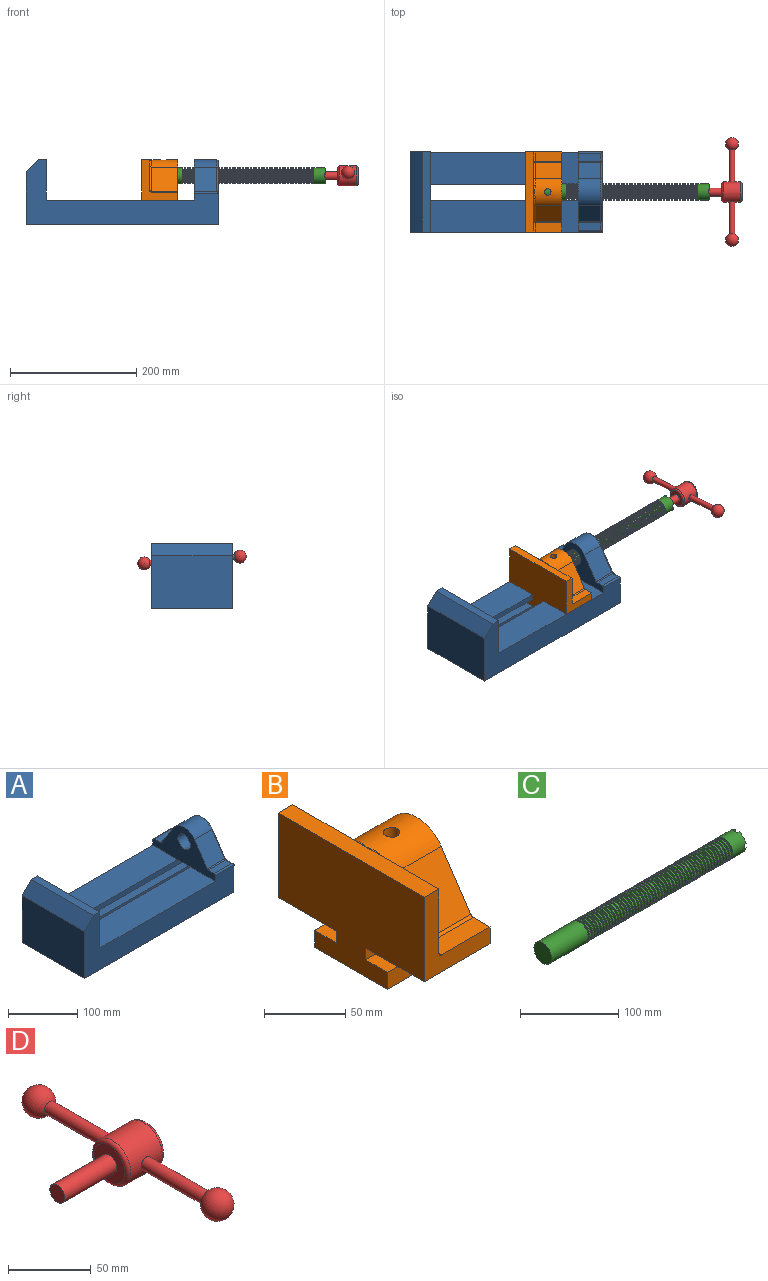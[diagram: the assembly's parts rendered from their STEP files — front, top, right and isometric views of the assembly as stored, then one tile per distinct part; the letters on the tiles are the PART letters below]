
ASSEMBLY  parts=4 mates=4
PART A: 39 faces, bbox 304.8x127x103.7 mm
  f0: plane 234.95x50.8mm, normal (0,0,1), area 11935.5mm2, adj f3,f8,f16,f26
  f1: plane 127x99.06mm, normal (1,0,0), area 7097.5mm2, adj f7,f8,f9,f14,f17,f18,f19,f20
  f2: plane 234.95x50.8mm, normal (0,0,1), area 11935.5mm2, adj f3,f9,f16,f27
  f3: plane 127x101.6mm, normal (1,0,0), area 9516.1mm2, adj f0,f2,f4,f7,f8,f9,f18,f19
  f4: plane 127x12.7mm, normal (0,0,1), area 1612.9mm2, adj f3,f5,f8,f9
  f5: plane 127x19.05mm, normal (-0.71,0,0.71), area 3421.5mm2, adj f4,f6,f8,f9
  f6: plane 127x82.55mm, normal (-1,0,0), area 10483.8mm2, adj f5,f7,f8,f9
  f7: plane 304.8x127mm, normal (0,0,-1), area 31774.1mm2, adj f1,f3,f6,f8,f9,f21,f22
  f8: plane 304.8x101.6mm, normal (0,-1,0), area 13834.6mm2, adj f0,f1,f3,f4,f5,f6,f7,f16
  f9: plane 304.8x101.6mm, normal (0,1,0), area 13834.6mm2, adj f1,f2,f3,f4,f5,f6,f7,f16
  f10: plane 35.56x11.98mm, normal (0,0,1), area 426mm2, adj f16,f28,f29,f30
  f11: plane 38.43x35.56mm, normal (0,0.83,0.56), area 1645.4mm2, adj f12,f16,f29,f32
  f12: cylinder r=25.4mm len=42.19mm, axis (1,0,0), area 1770.2mm2, adj f11,f13,f16,f33
  f13: plane 38.43x35.56mm, normal (0,-0.83,0.56), area 1645.4mm2, adj f12,f16,f34,f35
  f14: cylinder r=12.7mm len=38.1mm, axis (1,0,0), area 3040.2mm2, adj f1,f16
  f15: plane 35.56x11.98mm, normal (0,0,1), area 426mm2, adj f16,f34,f36,f38
  f16: plane 127x63.5mm, normal (-1,0,0), area 4155.5mm2, adj f0,f2,f8,f9,f10,f11,f12,f13
  f17: plane 38.1x25.4mm, normal (0,0,-1), area 967.7mm2, adj f1,f16,f26,f27
  f18: plane 273.05x19.05mm, normal (0,0,-1), area 5201.6mm2, adj f1,f3,f19,f26
  f19: plane 273.05x12.7mm, normal (0,1,0), area 3467.7mm2, adj f1,f3,f18,f20
  f20: plane 273.05x19.05mm, normal (0,0,1), area 5201.6mm2, adj f1,f3,f19,f21
  f21: plane 273.05x16.51mm, normal (0,1,0), area 4508.1mm2, adj f1,f3,f7,f20
  f22: plane 273.05x16.51mm, normal (0,-1,0), area 4508.1mm2, adj f1,f3,f7,f23
  f23: plane 273.05x19.05mm, normal (0,0,1), area 5201.6mm2, adj f1,f3,f22,f24
  f24: plane 273.05x12.7mm, normal (0,-1,0), area 3467.7mm2, adj f1,f3,f23,f25
  f25: plane 273.05x19.05mm, normal (0,0,-1), area 5201.6mm2, adj f1,f3,f24,f27
  f26: plane 273.05x8.89mm, normal (0,1,0), area 2427.4mm2, adj f0,f1,f3,f17,f18
  f27: plane 273.05x8.89mm, normal (0,-1,0), area 2427.4mm2, adj f1,f2,f3,f17,f25
  f28: cylinder r=2.54mm len=38.1mm, axis (1,0,0), area 148.3mm2, adj f9,f10,f16,f30
  f29: cylinder r=2.54mm len=35.56mm, axis (-1,0,0), area 88.5mm2, adj f10,f11,f16,f31
  f30: cylinder r=2.54mm len=14.52mm, axis (0,1,0), area 54.3mm2, adj f1,f10,f28,f31
  f31: torus R=5.08mm, axis (-1,0,0), area 13.5mm2, adj f1,f29,f30,f32
  f32: cylinder r=2.54mm len=39.84mm, axis (0,0.56,-0.83), area 184.6mm2, adj f1,f11,f31,f33
  f33: torus R=22.86mm, axis (-1,0,0), area 191.4mm2, adj f1,f12,f32,f35
  f34: cylinder r=2.54mm len=35.56mm, axis (-1,0,0), area 88.5mm2, adj f13,f15,f16,f37
  f35: cylinder r=2.54mm len=39.84mm, axis (0,0.56,0.83), area 184.6mm2, adj f1,f13,f33,f37
  f36: cylinder r=2.54mm len=38.1mm, axis (-1,0,0), area 148.3mm2, adj f8,f15,f16,f38
  f37: torus R=5.08mm, axis (-1,0,0), area 13.5mm2, adj f1,f34,f35,f38
  f38: cylinder r=2.54mm len=14.52mm, axis (0,1,0), area 54.3mm2, adj f1,f15,f36,f37
PART B: 36 faces, bbox 57.2x127x89 mm
  f0: plane 57.15x50.8mm, normal (0,0,-1), area 2903.2mm2, adj f6,f9,f10,f23
  f1: cylinder r=12.7mm len=44.45mm, axis (1,0,0), area 3464.3mm2, adj f6,f15,f16
  f2: plane 41.91x14.52mm, normal (0,0,1), area 608.5mm2, adj f6,f11,f24,f25
  f3: plane 51.86x48.26mm, normal (1,0,0), area 1495.7mm2, adj f8,f10,f31,f33,f35
  f4: plane 51.86x48.26mm, normal (1,0,0), area 1495.7mm2, adj f8,f11,f24,f28,f29
  f5: plane 57.15x50.8mm, normal (0,0,-1), area 2903.2mm2, adj f6,f9,f11,f22
  f6: plane 127x85.09mm, normal (1,0,0), area 5190.6mm2, adj f0,f1,f2,f5,f7,f10,f11,f12
  f7: plane 41.91x14.52mm, normal (0,0,1), area 608.5mm2, adj f6,f10,f30,f31
  f8: plane 127x12.7mm, normal (0,0,1), area 1612.9mm2, adj f3,f4,f9,f10,f11,f26,f34
  f9: plane 127x85.09mm, normal (-1,0,0), area 9096.8mm2, adj f0,f5,f8,f10,f11,f17,f18,f19
  f10: plane 63.5x57.15mm, normal (0,-1,0), area 1372.3mm2, adj f0,f3,f6,f7,f8,f9,f31
  f11: plane 63.5x57.15mm, normal (0,1,0), area 1372.3mm2, adj f2,f4,f5,f6,f8,f9,f24
  f12: plane 41.91x38.43mm, normal (0,-0.83,0.56), area 1939.2mm2, adj f6,f13,f30,f33
  f13: cylinder r=25.4mm len=44.45mm, axis (1,0,0), area 2026.5mm2, adj f6,f12,f14,f16,f26,f28,f34,f35
  f14: plane 41.91x38.43mm, normal (0,0.83,0.56), area 1939.2mm2, adj f6,f13,f25,f29
  f15: plane 25.4x25.4mm, normal (1,0,0), area 506.7mm2, adj f1
  f16: cylinder r=5.08mm len=13.76mm, axis (0,0,1), area 414mm2, adj f1,f13
  f17: plane 57.15x19.05mm, normal (0,0,1), area 1088.7mm2, adj f6,f9,f18,f23
  f18: plane 57.15x12.7mm, normal (0,-1,0), area 725.8mm2, adj f6,f9,f17,f19
  f19: plane 63.5x57.15mm, normal (0,0,-1), area 3629mm2, adj f6,f9,f18,f20
  f20: plane 57.15x12.7mm, normal (0,1,0), area 725.8mm2, adj f6,f9,f19,f21
  f21: plane 57.15x19.05mm, normal (0,0,1), area 1088.7mm2, adj f6,f9,f20,f22
  f22: plane 57.15x8.89mm, normal (0,1,0), area 508.1mm2, adj f5,f6,f9,f21
  f23: plane 57.15x8.89mm, normal (0,-1,0), area 508.1mm2, adj f0,f6,f9,f17
  f24: cylinder r=2.54mm len=14.52mm, axis (0,-1,0), area 57.9mm2, adj f2,f4,f11,f27
  f25: cylinder r=2.54mm len=41.91mm, axis (1,0,0), area 104.3mm2, adj f2,f6,f14,f27
  f26: bspline ~12.24x2.8mm, area 20.9mm2, adj f8,f13,f28
  f27: sphere r=2.54mm, area 6.3mm2, adj f24,f25,f29
  f28: torus R=27.94mm, axis (1,0,0), area 57.8mm2, adj f4,f13,f26,f29
  f29: cylinder r=2.54mm len=39.84mm, axis (0,-0.56,0.83), area 184.6mm2, adj f4,f14,f27,f28
  f30: cylinder r=2.54mm len=41.91mm, axis (1,0,0), area 104.3mm2, adj f6,f7,f12,f32
  f31: cylinder r=2.54mm len=14.52mm, axis (0,-1,0), area 57.9mm2, adj f3,f7,f10,f32
  f32: sphere r=2.54mm, area 6.3mm2, adj f30,f31,f33
  f33: cylinder r=2.54mm len=39.84mm, axis (0,-0.56,-0.83), area 184.6mm2, adj f3,f12,f32,f35
  f34: bspline ~12.24x2.8mm, area 20.9mm2, adj f8,f13,f35
  f35: torus R=27.94mm, axis (1,0,0), area 57.8mm2, adj f3,f13,f33,f34
PART C: 220 faces, bbox 279.4x25.4x25.4 mm
  f0: cylinder r=12.7mm len=25.4mm, axis (-1,0,0), area 1468.2mm2, adj f1,f2,f3,f5,f7,f208,f209,f210
  f1: plane 9.9x9.9mm, normal (1,0,0), area 62.3mm2, adj f0,f4,f213,f216
  f2: plane 9.9x9.9mm, normal (1,0,0), area 62.3mm2, adj f0,f4,f210,f218
  f3: plane 9.9x9.9mm, normal (1,0,0), area 62.3mm2, adj f0,f4,f209,f212
  f4: cylinder r=6.35mm len=25.4mm, axis (1,0,0), area 960.3mm2, adj f1,f2,f3,f5,f6,f208,f209,f210
  f5: plane 9.9x9.9mm, normal (1,0,0), area 62.3mm2, adj f0,f4,f215,f217
  f6: plane 12.7x12.7mm, normal (1,0,0), area 126.7mm2, adj f4
  f7: cone r=12.7mm half-angle=76deg, axis (1,0,0), area 188mm2, adj f0,f9
  f8: cone r=10.16mm half-angle=76deg, axis (-1,0,0), area 188mm2, adj f9,f10
  f9: cylinder r=10.16mm len=20.32mm, axis (1,0,0), area 81.1mm2, adj f7,f8
  f10: cylinder r=12.7mm len=25.4mm, axis (-1,0,0), area 131.7mm2, adj f8,f11
  f11: cone r=12.7mm half-angle=76deg, axis (1,0,0), area 188mm2, adj f10,f13
  f12: cone r=10.16mm half-angle=76deg, axis (-1,0,0), area 188mm2, adj f13,f14
  f13: cylinder r=10.16mm len=20.32mm, axis (1,0,0), area 81.1mm2, adj f11,f12
  f14: cylinder r=12.7mm len=25.4mm, axis (-1,0,0), area 131.7mm2, adj f12,f15
  f15: cone r=12.7mm half-angle=76deg, axis (1,0,0), area 188mm2, adj f14,f17
  f16: cone r=10.16mm half-angle=76deg, axis (-1,0,0), area 188mm2, adj f17,f18
  f17: cylinder r=10.16mm len=20.32mm, axis (1,0,0), area 81.1mm2, adj f15,f16
  f18: cylinder r=12.7mm len=25.4mm, axis (-1,0,0), area 131.7mm2, adj f16,f19
  f19: cone r=12.7mm half-angle=76deg, axis (1,0,0), area 188mm2, adj f18,f21
  f20: cone r=10.16mm half-angle=76deg, axis (-1,0,0), area 188mm2, adj f21,f22
  f21: cylinder r=10.16mm len=20.32mm, axis (1,0,0), area 81.1mm2, adj f19,f20
  f22: cylinder r=12.7mm len=25.4mm, axis (-1,0,0), area 131.7mm2, adj f20,f23
  f23: cone r=12.7mm half-angle=76deg, axis (1,0,0), area 188mm2, adj f22,f25
  f24: cone r=10.16mm half-angle=76deg, axis (-1,0,0), area 188mm2, adj f25,f26
  f25: cylinder r=10.16mm len=20.32mm, axis (1,0,0), area 81.1mm2, adj f23,f24
  f26: cylinder r=12.7mm len=25.4mm, axis (-1,0,0), area 131.7mm2, adj f24,f27
  f27: cone r=12.7mm half-angle=76deg, axis (1,0,0), area 188mm2, adj f26,f29
  f28: cone r=10.16mm half-angle=76deg, axis (-1,0,0), area 188mm2, adj f29,f30
  f29: cylinder r=10.16mm len=20.32mm, axis (1,0,0), area 81.1mm2, adj f27,f28
  f30: cylinder r=12.7mm len=25.4mm, axis (-1,0,0), area 131.7mm2, adj f28,f31
  f31: cone r=12.7mm half-angle=76deg, axis (1,0,0), area 188mm2, adj f30,f33
  f32: cone r=10.16mm half-angle=76deg, axis (-1,0,0), area 188mm2, adj f33,f34
  f33: cylinder r=10.16mm len=20.32mm, axis (1,0,0), area 81.1mm2, adj f31,f32
  f34: cylinder r=12.7mm len=25.4mm, axis (-1,0,0), area 131.7mm2, adj f32,f35
  f35: cone r=12.7mm half-angle=76deg, axis (1,0,0), area 188mm2, adj f34,f37
  f36: cone r=10.16mm half-angle=76deg, axis (-1,0,0), area 188mm2, adj f37,f38
  f37: cylinder r=10.16mm len=20.32mm, axis (1,0,0), area 81.1mm2, adj f35,f36
  f38: cylinder r=12.7mm len=25.4mm, axis (-1,0,0), area 131.7mm2, adj f36,f39
  f39: cone r=12.7mm half-angle=76deg, axis (1,0,0), area 188mm2, adj f38,f41
  f40: cone r=10.16mm half-angle=76deg, axis (-1,0,0), area 188mm2, adj f41,f42
  f41: cylinder r=10.16mm len=20.32mm, axis (1,0,0), area 81.1mm2, adj f39,f40
  f42: cylinder r=12.7mm len=25.4mm, axis (-1,0,0), area 131.7mm2, adj f40,f43
  f43: cone r=12.7mm half-angle=76deg, axis (1,0,0), area 188mm2, adj f42,f45
  f44: cone r=10.16mm half-angle=76deg, axis (-1,0,0), area 188mm2, adj f45,f46
  f45: cylinder r=10.16mm len=20.32mm, axis (1,0,0), area 81.1mm2, adj f43,f44
  f46: cylinder r=12.7mm len=25.4mm, axis (-1,0,0), area 131.7mm2, adj f44,f47
  f47: cone r=12.7mm half-angle=76deg, axis (1,0,0), area 188mm2, adj f46,f49
  f48: cone r=10.16mm half-angle=76deg, axis (-1,0,0), area 188mm2, adj f49,f50
  f49: cylinder r=10.16mm len=20.32mm, axis (1,0,0), area 81.1mm2, adj f47,f48
  f50: cylinder r=12.7mm len=25.4mm, axis (-1,0,0), area 131.7mm2, adj f48,f51
  f51: cone r=12.7mm half-angle=76deg, axis (1,0,0), area 188mm2, adj f50,f53
  f52: cone r=10.16mm half-angle=76deg, axis (-1,0,0), area 188mm2, adj f53,f54
  f53: cylinder r=10.16mm len=20.32mm, axis (1,0,0), area 81.1mm2, adj f51,f52
  f54: cylinder r=12.7mm len=25.4mm, axis (-1,0,0), area 131.7mm2, adj f52,f55
  f55: cone r=12.7mm half-angle=76deg, axis (1,0,0), area 188mm2, adj f54,f57
  f56: cone r=10.16mm half-angle=76deg, axis (-1,0,0), area 188mm2, adj f57,f58
  f57: cylinder r=10.16mm len=20.32mm, axis (1,0,0), area 81.1mm2, adj f55,f56
  f58: cylinder r=12.7mm len=25.4mm, axis (-1,0,0), area 131.7mm2, adj f56,f59
  f59: cone r=12.7mm half-angle=76deg, axis (1,0,0), area 188mm2, adj f58,f61
  f60: cone r=10.16mm half-angle=76deg, axis (-1,0,0), area 188mm2, adj f61,f62
  f61: cylinder r=10.16mm len=20.32mm, axis (1,0,0), area 81.1mm2, adj f59,f60
  f62: cylinder r=12.7mm len=25.4mm, axis (-1,0,0), area 131.7mm2, adj f60,f63
  f63: cone r=12.7mm half-angle=76deg, axis (1,0,0), area 188mm2, adj f62,f65
  f64: cone r=10.16mm half-angle=76deg, axis (-1,0,0), area 188mm2, adj f65,f66
  f65: cylinder r=10.16mm len=20.32mm, axis (1,0,0), area 81.1mm2, adj f63,f64
  f66: cylinder r=12.7mm len=25.4mm, axis (-1,0,0), area 131.7mm2, adj f64,f67
  f67: cone r=12.7mm half-angle=76deg, axis (1,0,0), area 188mm2, adj f66,f69
  f68: cone r=10.16mm half-angle=76deg, axis (-1,0,0), area 188mm2, adj f69,f70
  f69: cylinder r=10.16mm len=20.32mm, axis (1,0,0), area 81.1mm2, adj f67,f68
  f70: cylinder r=12.7mm len=25.4mm, axis (-1,0,0), area 131.7mm2, adj f68,f71
  f71: cone r=12.7mm half-angle=76deg, axis (1,0,0), area 188mm2, adj f70,f73
  f72: cone r=10.16mm half-angle=76deg, axis (-1,0,0), area 188mm2, adj f73,f74
  f73: cylinder r=10.16mm len=20.32mm, axis (1,0,0), area 81.1mm2, adj f71,f72
  f74: cylinder r=12.7mm len=25.4mm, axis (-1,0,0), area 131.7mm2, adj f72,f75
  f75: cone r=12.7mm half-angle=76deg, axis (1,0,0), area 188mm2, adj f74,f77
  f76: cone r=10.16mm half-angle=76deg, axis (-1,0,0), area 188mm2, adj f77,f78
  f77: cylinder r=10.16mm len=20.32mm, axis (1,0,0), area 81.1mm2, adj f75,f76
  f78: cylinder r=12.7mm len=25.4mm, axis (-1,0,0), area 131.7mm2, adj f76,f79
  f79: cone r=12.7mm half-angle=76deg, axis (1,0,0), area 188mm2, adj f78,f81
  f80: cone r=10.16mm half-angle=76deg, axis (-1,0,0), area 188mm2, adj f81,f82
  f81: cylinder r=10.16mm len=20.32mm, axis (1,0,0), area 81.1mm2, adj f79,f80
  f82: cylinder r=12.7mm len=25.4mm, axis (-1,0,0), area 131.7mm2, adj f80,f83
  f83: cone r=12.7mm half-angle=76deg, axis (1,0,0), area 188mm2, adj f82,f85
  f84: cone r=10.16mm half-angle=76deg, axis (-1,0,0), area 188mm2, adj f85,f86
  f85: cylinder r=10.16mm len=20.32mm, axis (1,0,0), area 81.1mm2, adj f83,f84
  f86: cylinder r=12.7mm len=25.4mm, axis (-1,0,0), area 131.7mm2, adj f84,f87
  f87: cone r=12.7mm half-angle=76deg, axis (1,0,0), area 188mm2, adj f86,f89
  f88: cone r=10.16mm half-angle=76deg, axis (-1,0,0), area 188mm2, adj f89,f90
  f89: cylinder r=10.16mm len=20.32mm, axis (1,0,0), area 81.1mm2, adj f87,f88
  f90: cylinder r=12.7mm len=25.4mm, axis (-1,0,0), area 131.7mm2, adj f88,f91
  f91: cone r=12.7mm half-angle=76deg, axis (1,0,0), area 188mm2, adj f90,f93
  f92: cone r=10.16mm half-angle=76deg, axis (-1,0,0), area 188mm2, adj f93,f94
  f93: cylinder r=10.16mm len=20.32mm, axis (1,0,0), area 81.1mm2, adj f91,f92
  f94: cylinder r=12.7mm len=25.4mm, axis (-1,0,0), area 131.7mm2, adj f92,f95
  f95: cone r=12.7mm half-angle=76deg, axis (1,0,0), area 188mm2, adj f94,f97
  f96: cone r=10.16mm half-angle=76deg, axis (-1,0,0), area 188mm2, adj f97,f98
  f97: cylinder r=10.16mm len=20.32mm, axis (1,0,0), area 81.1mm2, adj f95,f96
  f98: cylinder r=12.7mm len=25.4mm, axis (-1,0,0), area 131.7mm2, adj f96,f99
  f99: cone r=12.7mm half-angle=76deg, axis (1,0,0), area 188mm2, adj f98,f101
  f100: cone r=10.16mm half-angle=76deg, axis (-1,0,0), area 188mm2, adj f101,f102
  f101: cylinder r=10.16mm len=20.32mm, axis (1,0,0), area 81.1mm2, adj f99,f100
  f102: cylinder r=12.7mm len=25.4mm, axis (-1,0,0), area 131.7mm2, adj f100,f103
  f103: cone r=12.7mm half-angle=76deg, axis (1,0,0), area 188mm2, adj f102,f105
  f104: cone r=10.16mm half-angle=76deg, axis (-1,0,0), area 188mm2, adj f105,f106
  f105: cylinder r=10.16mm len=20.32mm, axis (1,0,0), area 81.1mm2, adj f103,f104
  f106: cylinder r=12.7mm len=25.4mm, axis (-1,0,0), area 131.7mm2, adj f104,f107
  f107: cone r=12.7mm half-angle=76deg, axis (1,0,0), area 188mm2, adj f106,f109
  f108: cone r=10.16mm half-angle=76deg, axis (-1,0,0), area 188mm2, adj f109,f110
  f109: cylinder r=10.16mm len=20.32mm, axis (1,0,0), area 81.1mm2, adj f107,f108
  f110: cylinder r=12.7mm len=25.4mm, axis (-1,0,0), area 131.7mm2, adj f108,f111
  f111: cone r=12.7mm half-angle=76deg, axis (1,0,0), area 188mm2, adj f110,f113
  f112: cone r=10.16mm half-angle=76deg, axis (-1,0,0), area 188mm2, adj f113,f114
  f113: cylinder r=10.16mm len=20.32mm, axis (1,0,0), area 81.1mm2, adj f111,f112
  f114: cylinder r=12.7mm len=25.4mm, axis (-1,0,0), area 131.7mm2, adj f112,f115
  f115: cone r=12.7mm half-angle=76deg, axis (1,0,0), area 188mm2, adj f114,f117
  f116: cone r=10.16mm half-angle=76deg, axis (-1,0,0), area 188mm2, adj f117,f118
  f117: cylinder r=10.16mm len=20.32mm, axis (1,0,0), area 81.1mm2, adj f115,f116
  f118: cylinder r=12.7mm len=25.4mm, axis (-1,0,0), area 131.7mm2, adj f116,f119
  f119: cone r=12.7mm half-angle=76deg, axis (1,0,0), area 188mm2, adj f118,f121
  f120: cone r=10.16mm half-angle=76deg, axis (-1,0,0), area 188mm2, adj f121,f122
  f121: cylinder r=10.16mm len=20.32mm, axis (1,0,0), area 81.1mm2, adj f119,f120
  f122: cylinder r=12.7mm len=25.4mm, axis (-1,0,0), area 131.7mm2, adj f120,f123
  f123: cone r=12.7mm half-angle=76deg, axis (1,0,0), area 188mm2, adj f122,f125
  f124: cone r=10.16mm half-angle=76deg, axis (-1,0,0), area 188mm2, adj f125,f126
  f125: cylinder r=10.16mm len=20.32mm, axis (1,0,0), area 81.1mm2, adj f123,f124
  f126: cylinder r=12.7mm len=25.4mm, axis (-1,0,0), area 131.7mm2, adj f124,f127
  f127: cone r=12.7mm half-angle=76deg, axis (1,0,0), area 188mm2, adj f126,f129
  f128: cone r=10.16mm half-angle=76deg, axis (-1,0,0), area 188mm2, adj f129,f130
  f129: cylinder r=10.16mm len=20.32mm, axis (1,0,0), area 81.1mm2, adj f127,f128
  f130: cylinder r=12.7mm len=25.4mm, axis (-1,0,0), area 131.7mm2, adj f128,f131
  f131: cone r=12.7mm half-angle=76deg, axis (1,0,0), area 188mm2, adj f130,f133
  f132: cone r=10.16mm half-angle=76deg, axis (-1,0,0), area 188mm2, adj f133,f134
  f133: cylinder r=10.16mm len=20.32mm, axis (1,0,0), area 81.1mm2, adj f131,f132
  f134: cylinder r=12.7mm len=25.4mm, axis (-1,0,0), area 131.7mm2, adj f132,f135
  f135: cone r=12.7mm half-angle=76deg, axis (1,0,0), area 188mm2, adj f134,f137
  f136: cone r=10.16mm half-angle=76deg, axis (-1,0,0), area 188mm2, adj f137,f138
  f137: cylinder r=10.16mm len=20.32mm, axis (1,0,0), area 81.1mm2, adj f135,f136
  f138: cylinder r=12.7mm len=25.4mm, axis (-1,0,0), area 131.7mm2, adj f136,f139
  f139: cone r=12.7mm half-angle=76deg, axis (1,0,0), area 188mm2, adj f138,f141
  f140: cone r=10.16mm half-angle=76deg, axis (-1,0,0), area 188mm2, adj f141,f142
  f141: cylinder r=10.16mm len=20.32mm, axis (1,0,0), area 81.1mm2, adj f139,f140
  f142: cylinder r=12.7mm len=25.4mm, axis (-1,0,0), area 131.7mm2, adj f140,f143
  f143: cone r=12.7mm half-angle=76deg, axis (1,0,0), area 188mm2, adj f142,f145
  f144: cone r=10.16mm half-angle=76deg, axis (-1,0,0), area 188mm2, adj f145,f146
  f145: cylinder r=10.16mm len=20.32mm, axis (1,0,0), area 81.1mm2, adj f143,f144
  f146: cylinder r=12.7mm len=25.4mm, axis (-1,0,0), area 131.7mm2, adj f144,f147
  f147: cone r=12.7mm half-angle=76deg, axis (1,0,0), area 188mm2, adj f146,f149
  f148: cone r=10.16mm half-angle=76deg, axis (-1,0,0), area 188mm2, adj f149,f150
  f149: cylinder r=10.16mm len=20.32mm, axis (1,0,0), area 81.1mm2, adj f147,f148
  f150: cylinder r=12.7mm len=25.4mm, axis (-1,0,0), area 131.7mm2, adj f148,f151
  f151: cone r=12.7mm half-angle=76deg, axis (1,0,0), area 188mm2, adj f150,f153
  f152: cone r=10.16mm half-angle=76deg, axis (-1,0,0), area 188mm2, adj f153,f154
  f153: cylinder r=10.16mm len=20.32mm, axis (1,0,0), area 81.1mm2, adj f151,f152
  f154: cylinder r=12.7mm len=25.4mm, axis (-1,0,0), area 131.7mm2, adj f152,f155
  f155: cone r=12.7mm half-angle=76deg, axis (1,0,0), area 188mm2, adj f154,f157
  f156: cone r=10.16mm half-angle=76deg, axis (-1,0,0), area 188mm2, adj f157,f158
  f157: cylinder r=10.16mm len=20.32mm, axis (1,0,0), area 81.1mm2, adj f155,f156
  f158: cylinder r=12.7mm len=25.4mm, axis (-1,0,0), area 131.7mm2, adj f156,f159
  f159: cone r=12.7mm half-angle=76deg, axis (1,0,0), area 188mm2, adj f158,f161
  f160: cone r=10.16mm half-angle=76deg, axis (-1,0,0), area 188mm2, adj f161,f162
  f161: cylinder r=10.16mm len=20.32mm, axis (1,0,0), area 81.1mm2, adj f159,f160
  f162: cylinder r=12.7mm len=25.4mm, axis (-1,0,0), area 131.7mm2, adj f160,f163
  f163: cone r=12.7mm half-angle=76deg, axis (1,0,0), area 188mm2, adj f162,f165
  f164: cone r=10.16mm half-angle=76deg, axis (-1,0,0), area 188mm2, adj f165,f166
  f165: cylinder r=10.16mm len=20.32mm, axis (1,0,0), area 81.1mm2, adj f163,f164
  f166: cylinder r=12.7mm len=25.4mm, axis (-1,0,0), area 131.7mm2, adj f164,f167
  f167: cone r=12.7mm half-angle=76deg, axis (1,0,0), area 188mm2, adj f166,f169
  f168: cone r=10.16mm half-angle=76deg, axis (-1,0,0), area 188mm2, adj f169,f170
  f169: cylinder r=10.16mm len=20.32mm, axis (1,0,0), area 81.1mm2, adj f167,f168
  f170: cylinder r=12.7mm len=25.4mm, axis (-1,0,0), area 131.7mm2, adj f168,f171
  f171: cone r=12.7mm half-angle=76deg, axis (1,0,0), area 188mm2, adj f170,f173
  f172: cone r=10.16mm half-angle=76deg, axis (-1,0,0), area 188mm2, adj f173,f174
  f173: cylinder r=10.16mm len=20.32mm, axis (1,0,0), area 81.1mm2, adj f171,f172
  f174: cylinder r=12.7mm len=25.4mm, axis (-1,0,0), area 131.7mm2, adj f172,f175
  f175: cone r=12.7mm half-angle=76deg, axis (1,0,0), area 188mm2, adj f174,f177
  f176: cone r=10.16mm half-angle=76deg, axis (-1,0,0), area 188mm2, adj f177,f178
  f177: cylinder r=10.16mm len=20.32mm, axis (1,0,0), area 81.1mm2, adj f175,f176
  f178: cylinder r=12.7mm len=25.4mm, axis (-1,0,0), area 131.7mm2, adj f176,f179
  f179: cone r=12.7mm half-angle=76deg, axis (1,0,0), area 188mm2, adj f178,f181
  f180: cone r=10.16mm half-angle=76deg, axis (-1,0,0), area 188mm2, adj f181,f182
  f181: cylinder r=10.16mm len=20.32mm, axis (1,0,0), area 81.1mm2, adj f179,f180
  f182: cylinder r=12.7mm len=25.4mm, axis (-1,0,0), area 131.7mm2, adj f180,f183
  f183: cone r=12.7mm half-angle=76deg, axis (1,0,0), area 188mm2, adj f182,f185
  f184: cone r=10.16mm half-angle=76deg, axis (-1,0,0), area 188mm2, adj f185,f186
  f185: cylinder r=10.16mm len=20.32mm, axis (1,0,0), area 81.1mm2, adj f183,f184
  f186: cylinder r=12.7mm len=25.4mm, axis (-1,0,0), area 131.7mm2, adj f184,f187
  f187: cone r=12.7mm half-angle=76deg, axis (1,0,0), area 188mm2, adj f186,f189
  f188: cone r=10.16mm half-angle=76deg, axis (-1,0,0), area 188mm2, adj f189,f190
  f189: cylinder r=10.16mm len=20.32mm, axis (1,0,0), area 81.1mm2, adj f187,f188
  f190: cylinder r=12.7mm len=25.4mm, axis (-1,0,0), area 131.7mm2, adj f188,f191
  f191: cone r=12.7mm half-angle=76deg, axis (1,0,0), area 188mm2, adj f190,f193
  f192: cone r=10.16mm half-angle=76deg, axis (-1,0,0), area 188mm2, adj f193,f194
  f193: cylinder r=10.16mm len=20.32mm, axis (1,0,0), area 81.1mm2, adj f191,f192
  f194: cylinder r=12.7mm len=25.4mm, axis (-1,0,0), area 131.7mm2, adj f192,f195
  f195: cone r=12.7mm half-angle=76deg, axis (1,0,0), area 188mm2, adj f194,f197
  f196: cone r=10.16mm half-angle=76deg, axis (-1,0,0), area 188mm2, adj f197,f198
  f197: cylinder r=10.16mm len=20.32mm, axis (1,0,0), area 81.1mm2, adj f195,f196
  f198: cylinder r=12.7mm len=25.4mm, axis (-1,0,0), area 131.7mm2, adj f196,f199
  f199: cone r=12.7mm half-angle=76deg, axis (1,0,0), area 188mm2, adj f198,f201
  f200: cone r=10.16mm half-angle=76deg, axis (-1,0,0), area 188mm2, adj f201,f202
  f201: cylinder r=10.16mm len=20.32mm, axis (1,0,0), area 81.1mm2, adj f199,f200
  f202: cylinder r=12.7mm len=25.4mm, axis (-1,0,0), area 131.7mm2, adj f200,f203
  f203: cone r=12.7mm half-angle=76deg, axis (1,0,0), area 188mm2, adj f202,f205
  f204: cone r=10.16mm half-angle=76deg, axis (-1,0,0), area 188mm2, adj f205,f207
  f205: cylinder r=10.16mm len=20.32mm, axis (1,0,0), area 81.1mm2, adj f203,f204
  f206: plane 25.4x25.4mm, normal (-1,0,0), area 506.7mm2, adj f207
  f207: cylinder r=12.7mm len=52.45mm, axis (-1,0,0), area 4185.4mm2, adj f204,f206
  f208: plane 6.88x5.08mm, normal (1,0,0), area 32.7mm2, adj f0,f4,f209,f210
  f209: plane 6.62x2.54mm, normal (0,-1,0), area 16.8mm2, adj f0,f3,f4,f208
  f210: plane 6.62x2.54mm, normal (0,1,0), area 16.8mm2, adj f0,f2,f4,f208
  f211: plane 6.88x5.08mm, normal (1,0,0), area 32.7mm2, adj f0,f4,f212,f213
  f212: plane 6.62x2.54mm, normal (0,0,1), area 16.8mm2, adj f0,f3,f4,f211
  f213: plane 6.62x2.54mm, normal (0,0,-1), area 16.8mm2, adj f0,f1,f4,f211
  f214: plane 6.88x5.08mm, normal (1,0,0), area 32.7mm2, adj f0,f4,f215,f216
  f215: plane 6.62x2.54mm, normal (0,1,0), area 16.8mm2, adj f0,f4,f5,f214
  f216: plane 6.62x2.54mm, normal (0,-1,0), area 16.8mm2, adj f0,f1,f4,f214
  f217: plane 6.62x2.54mm, normal (0,0,-1), area 16.8mm2, adj f0,f4,f5,f219
  f218: plane 6.62x2.54mm, normal (0,0,1), area 16.8mm2, adj f0,f2,f4,f219
  f219: plane 6.88x5.08mm, normal (1,0,0), area 32.7mm2, adj f0,f4,f217,f218
PART D: 11 faces, bbox 76.2x172.7x34.4 mm
  f0: sphere r=10.16mm, area 1231.8mm2, adj f1
  f1: cylinder r=4.45mm len=51.82mm, axis (0,1,0), area 1438.5mm2, adj f0,f4
  f2: sphere r=10.16mm, area 1231.8mm2, adj f3
  f3: cylinder r=4.45mm len=51.82mm, axis (0,1,0), area 1438.5mm2, adj f2,f4
  f4: cylinder r=15.88mm len=31.75mm, axis (-1,0,0), area 2534.7mm2, adj f1,f3,f9,f10
  f5: cylinder r=6.35mm len=44.45mm, axis (-1,0,0), area 1773.5mm2, adj f6,f8
  f6: plane 12.7x12.7mm, normal (-1,0,0), area 126.7mm2, adj f5
  f7: plane 26.67x26.67mm, normal (1,0,0), area 558.6mm2, adj f10
  f8: plane 26.67x26.67mm, normal (-1,0,0), area 432mm2, adj f5,f9
  f9: torus R=13.33mm, axis (1,0,0), area 374.8mm2, adj f4,f8
  f10: torus R=13.33mm, axis (1,0,0), area 374.8mm2, adj f4,f7
PLACE A t=(0.76,0,0)mm fixed
PLACE B t=(152.62,0,0)mm
PLACE C rot(axis=(1,0,0),176deg) t=(152.62,5.35,152.21)mm
PLACE D rot(axis=(-1,0,0),4deg) t=(152.62,-5.35,0.19)mm
MATE revolute C.f7 <-> B.f28  axis (-1,0,0) through (-107.73,0,76.2)mm
MATE fastened D.f5 <-> C.f4  axis (-1,0,0) through (146.27,0,76.2)mm
MATE cylindrical C.f7 <-> A.f12  axis (-1,0,0) through (-81.5,0,76.2)mm
MATE slider B.f9 <-> A.f3  axis (-1,0,0) through (-120.43,-63.5,38.1)mm
